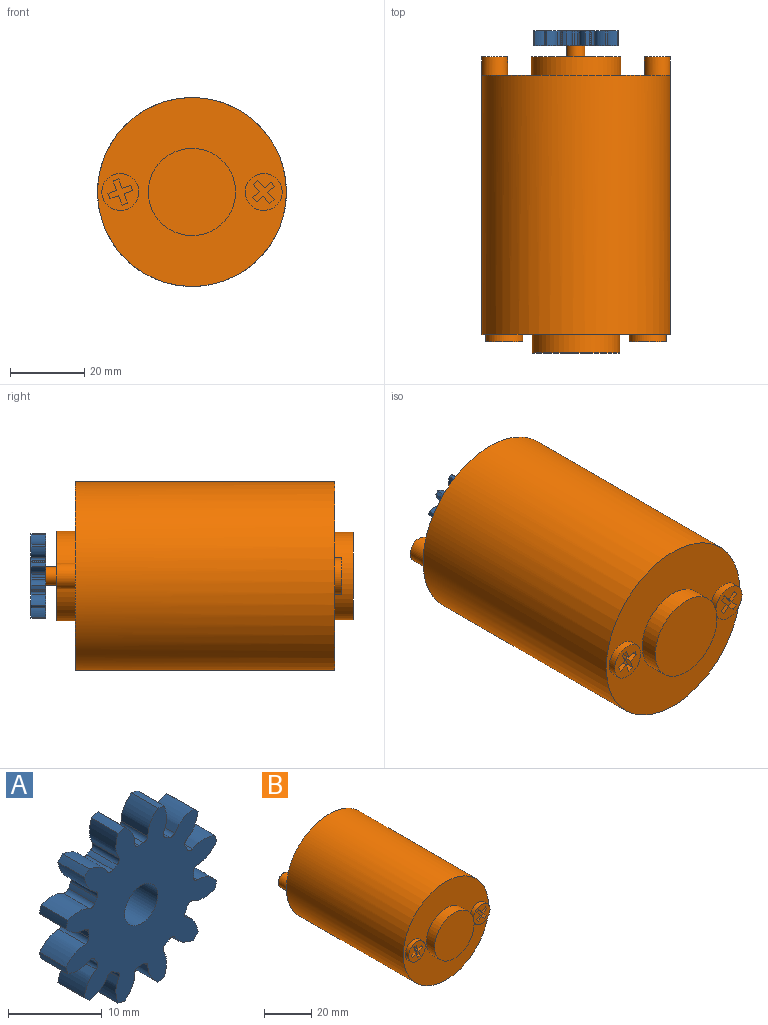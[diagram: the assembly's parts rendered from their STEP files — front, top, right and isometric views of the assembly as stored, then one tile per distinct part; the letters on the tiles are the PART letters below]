
ASSEMBLY  parts=2 mates=1
PART A: 75 faces, bbox 22.8x4x22.8 mm
  f0: extruded ~4x2.94mm, area 13.7mm2, adj f48,f49,f50,f51
  f1: cylinder r=7.92mm len=4mm, axis (0,1,0), area 2.8mm2, adj f49,f50,f51,f52
  f2: extruded ~4x2.94mm, area 13.7mm2, adj f3,f49,f50,f52
  f3: cylinder r=11.67mm len=4mm, axis (0,1,0), area 4.1mm2, adj f2,f4,f49,f50
  f4: extruded ~4x3.32mm, area 13.7mm2, adj f3,f49,f50,f53
  f5: cylinder r=7.92mm len=4mm, axis (0,1,0), area 2.8mm2, adj f49,f50,f53,f54
  f6: extruded ~4x2.8mm, area 13.7mm2, adj f7,f49,f50,f54
  f7: cylinder r=11.67mm len=4mm, axis (0,1,0), area 4.1mm2, adj f6,f8,f49,f50
  f8: extruded ~4x2.8mm, area 13.7mm2, adj f7,f49,f50,f55
  f9: cylinder r=7.92mm len=4mm, axis (0,1,0), area 2.8mm2, adj f49,f50,f55,f56
  f10: extruded ~4x3.32mm, area 13.7mm2, adj f11,f49,f50,f56
  f11: cylinder r=11.67mm len=4mm, axis (0,1,0), area 4.1mm2, adj f10,f12,f49,f50
  f12: extruded ~4x2.94mm, area 13.7mm2, adj f11,f49,f50,f57
  f13: cylinder r=7.92mm len=4mm, axis (0,1,0), area 2.8mm2, adj f49,f50,f57,f58
  f14: extruded ~4x2.94mm, area 13.7mm2, adj f15,f49,f50,f58
  f15: cylinder r=11.67mm len=4mm, axis (0,1,0), area 4.1mm2, adj f14,f16,f49,f50
  f16: extruded ~4x3.32mm, area 13.7mm2, adj f15,f49,f50,f59
  f17: cylinder r=7.92mm len=4mm, axis (0,1,0), area 2.8mm2, adj f49,f50,f59,f60
  f18: extruded ~4x2.8mm, area 13.7mm2, adj f19,f49,f50,f60
  f19: cylinder r=11.67mm len=4mm, axis (0,1,0), area 4.1mm2, adj f18,f20,f49,f50
  f20: extruded ~4x2.8mm, area 13.7mm2, adj f19,f49,f50,f61
  f21: cylinder r=7.92mm len=4mm, axis (0,1,0), area 2.8mm2, adj f49,f50,f61,f62
  f22: extruded ~4x3.32mm, area 13.7mm2, adj f23,f49,f50,f62
  f23: cylinder r=11.67mm len=4mm, axis (0,1,0), area 4.1mm2, adj f22,f24,f49,f50
  f24: extruded ~4x2.94mm, area 13.7mm2, adj f23,f49,f50,f63
  f25: cylinder r=7.92mm len=4mm, axis (0,1,0), area 2.8mm2, adj f49,f50,f63,f64
  f26: extruded ~4x2.94mm, area 13.7mm2, adj f27,f49,f50,f64
  f27: cylinder r=11.67mm len=4mm, axis (0,1,0), area 4.1mm2, adj f26,f28,f49,f50
  f28: extruded ~4x3.32mm, area 13.7mm2, adj f27,f49,f50,f65
  f29: cylinder r=7.92mm len=4mm, axis (0,1,0), area 2.8mm2, adj f49,f50,f65,f66
  f30: extruded ~4x2.8mm, area 13.7mm2, adj f31,f49,f50,f66
  f31: cylinder r=11.67mm len=4mm, axis (0,1,0), area 4.1mm2, adj f30,f32,f49,f50
  f32: extruded ~4x2.8mm, area 13.7mm2, adj f31,f49,f50,f67
  f33: cylinder r=7.92mm len=4mm, axis (0,1,0), area 2.8mm2, adj f49,f50,f67,f68
  f34: extruded ~4x3.32mm, area 13.7mm2, adj f35,f49,f50,f68
  f35: cylinder r=11.67mm len=4mm, axis (0,1,0), area 4.1mm2, adj f34,f36,f49,f50
  f36: extruded ~4x2.94mm, area 13.7mm2, adj f35,f49,f50,f69
  f37: cylinder r=7.92mm len=4mm, axis (0,1,0), area 2.8mm2, adj f49,f50,f69,f70
  f38: extruded ~4x2.94mm, area 13.7mm2, adj f39,f49,f50,f70
  f39: cylinder r=11.67mm len=4mm, axis (0,1,0), area 4.1mm2, adj f38,f40,f49,f50
  f40: extruded ~4x3.32mm, area 13.7mm2, adj f39,f49,f50,f71
  f41: cylinder r=7.92mm len=4mm, axis (0,1,0), area 2.8mm2, adj f49,f50,f71,f72
  f42: extruded ~4x2.8mm, area 13.7mm2, adj f43,f49,f50,f72
  f43: cylinder r=11.67mm len=4mm, axis (0,1,0), area 4.1mm2, adj f42,f44,f49,f50
  f44: extruded ~4x2.8mm, area 13.7mm2, adj f43,f49,f50,f73
  f45: cylinder r=7.92mm len=4mm, axis (0,1,0), area 2.8mm2, adj f49,f50,f73,f74
  f46: extruded ~4x3.32mm, area 13.7mm2, adj f48,f49,f50,f74
  f47: cylinder r=2.5mm len=5mm, axis (0,1,0), area 62.8mm2, adj f49,f50
  f48: cylinder r=11.67mm len=4mm, axis (0,1,0), area 4.1mm2, adj f0,f46,f49,f50
  f49: plane 22.85x22.85mm, normal (0,-1,0), area 282.5mm2, adj f0,f1,f2,f3,f4,f5,f6,f7
  f50: plane 22.85x22.85mm, normal (0,1,0), area 282.5mm2, adj f0,f1,f2,f3,f4,f5,f6,f7
  f51: cylinder r=0.61mm len=4mm, axis (0,1,0), area 3.7mm2, adj f0,f1,f49,f50
  f52: cylinder r=0.61mm len=4mm, axis (0,1,0), area 3.7mm2, adj f1,f2,f49,f50
  f53: cylinder r=0.61mm len=4mm, axis (0,1,0), area 3.7mm2, adj f4,f5,f49,f50
  f54: cylinder r=0.61mm len=4mm, axis (0,1,0), area 3.7mm2, adj f5,f6,f49,f50
  f55: cylinder r=0.61mm len=4mm, axis (0,1,0), area 3.7mm2, adj f8,f9,f49,f50
  f56: cylinder r=0.61mm len=4mm, axis (0,1,0), area 3.7mm2, adj f9,f10,f49,f50
  f57: cylinder r=0.61mm len=4mm, axis (0,1,0), area 3.7mm2, adj f12,f13,f49,f50
  f58: cylinder r=0.61mm len=4mm, axis (0,1,0), area 3.7mm2, adj f13,f14,f49,f50
  f59: cylinder r=0.61mm len=4mm, axis (0,1,0), area 3.7mm2, adj f16,f17,f49,f50
  f60: cylinder r=0.61mm len=4mm, axis (0,1,0), area 3.7mm2, adj f17,f18,f49,f50
  f61: cylinder r=0.61mm len=4mm, axis (0,1,0), area 3.7mm2, adj f20,f21,f49,f50
  f62: cylinder r=0.61mm len=4mm, axis (0,1,0), area 3.7mm2, adj f21,f22,f49,f50
  f63: cylinder r=0.61mm len=4mm, axis (0,1,0), area 3.7mm2, adj f24,f25,f49,f50
  f64: cylinder r=0.61mm len=4mm, axis (0,1,0), area 3.7mm2, adj f25,f26,f49,f50
  f65: cylinder r=0.61mm len=4mm, axis (0,1,0), area 3.7mm2, adj f28,f29,f49,f50
  f66: cylinder r=0.61mm len=4mm, axis (0,1,0), area 3.7mm2, adj f29,f30,f49,f50
  f67: cylinder r=0.61mm len=4mm, axis (0,1,0), area 3.7mm2, adj f32,f33,f49,f50
  f68: cylinder r=0.61mm len=4mm, axis (0,1,0), area 3.7mm2, adj f33,f34,f49,f50
  f69: cylinder r=0.61mm len=4mm, axis (0,1,0), area 3.7mm2, adj f36,f37,f49,f50
  f70: cylinder r=0.61mm len=4mm, axis (0,1,0), area 3.7mm2, adj f37,f38,f49,f50
  f71: cylinder r=0.61mm len=4mm, axis (0,1,0), area 3.7mm2, adj f40,f41,f49,f50
  f72: cylinder r=0.61mm len=4mm, axis (0,1,0), area 3.7mm2, adj f41,f42,f49,f50
  f73: cylinder r=0.61mm len=4mm, axis (0,1,0), area 3.7mm2, adj f44,f45,f49,f50
  f74: cylinder r=0.61mm len=4mm, axis (0,1,0), area 3.7mm2, adj f45,f46,f49,f50
PART B: 43 faces, bbox 51x87x51 mm
  f0: plane 51x51mm, normal (0,-1,0), area 1449.5mm2, adj f1,f3,f24,f40
  f1: cylinder r=25.5mm len=70mm, axis (0,1,0), area 11215.5mm2, adj f0,f2
  f2: plane 51x51mm, normal (0,1,0), area 1507.5mm2, adj f1,f5,f7,f9
  f3: cylinder r=11.79mm len=23.58mm, axis (0,1,0), area 370.4mm2, adj f0,f4
  f4: plane 23.58x23.58mm, normal (0,-1,0), area 436.8mm2, adj f3
  f5: cylinder r=12.08mm len=24.16mm, axis (0,-1,0), area 379.5mm2, adj f2,f6
  f6: plane 24.16x24.16mm, normal (0,1,0), area 438.7mm2, adj f5,f11
  f7: cylinder r=3.5mm len=7mm, axis (0,-1,0), area 110mm2, adj f2,f8
  f8: plane 7x7mm, normal (0,1,0), area 38.5mm2, adj f7
  f9: cylinder r=3.5mm len=7mm, axis (0,-1,0), area 110mm2, adj f2,f10
  f10: plane 7x7mm, normal (0,1,0), area 38.5mm2, adj f9
  f11: cylinder r=2.5mm len=7mm, axis (0,-1,0), area 110mm2, adj f6,f12
  f12: plane 5x5mm, normal (0,1,0), area 19.6mm2, adj f11
  f13: plane 2x1.16mm, normal (-0.77,0,-0.64), area 3mm2, adj f14,f25,f26,f27
  f14: plane 2x1.91mm, normal (-0.64,0,0.77), area 5mm2, adj f13,f15,f26,f27
  f15: plane 2.09x2mm, normal (-0.77,0,-0.64), area 5.4mm2, adj f14,f16,f26,f27
  f16: plane 2x1.21mm, normal (-0.64,0,0.77), area 3.2mm2, adj f15,f17,f26,f27
  f17: plane 2.09x2mm, normal (0.77,0,0.64), area 5.4mm2, adj f16,f18,f26,f27
  f18: plane 2x1.91mm, normal (-0.64,0,0.77), area 5mm2, adj f17,f19,f26,f27
  f19: plane 2x1.16mm, normal (0.77,0,0.64), area 3mm2, adj f18,f20,f26,f27
  f20: plane 2x1.91mm, normal (0.64,0,-0.77), area 5mm2, adj f19,f21,f26,f27
  f21: plane 2.09x2mm, normal (0.77,0,0.64), area 5.4mm2, adj f20,f22,f26,f27
  f22: plane 2x1.21mm, normal (0.64,0,-0.77), area 3.2mm2, adj f21,f23,f26,f27
  f23: plane 2.09x2mm, normal (-0.77,0,-0.64), area 5.4mm2, adj f22,f25,f26,f27
  f24: cylinder r=4.99mm len=9.98mm, axis (0,1,0), area 62.7mm2, adj f0,f26
  f25: plane 2x1.91mm, normal (0.64,0,-0.77), area 5mm2, adj f13,f23,f26,f27
  f26: plane 9.98x9.98mm, normal (0,-1,0), area 59.8mm2, adj f13,f14,f15,f16,f17,f18,f19,f20
  f27: plane 6.34x6.01mm, normal (0,-1,0), area 18.5mm2, adj f13,f14,f15,f16,f17,f18,f19,f20
  f28: plane 2.35x2mm, normal (-0.34,0,0.94), area 5mm2, adj f29,f39,f41,f42
  f29: plane 2x1.42mm, normal (0.94,0,0.34), area 3mm2, adj f28,f30,f41,f42
  f30: plane 2.35x2mm, normal (0.34,0,-0.94), area 5mm2, adj f29,f31,f41,f42
  f31: plane 2.56x2mm, normal (0.94,0,0.34), area 5.4mm2, adj f30,f32,f41,f42
  f32: plane 2x1.48mm, normal (0.34,0,-0.94), area 3.2mm2, adj f31,f33,f41,f42
  f33: plane 2.56x2mm, normal (-0.94,0,-0.34), area 5.4mm2, adj f32,f34,f41,f42
  f34: plane 2.35x2mm, normal (0.34,0,-0.94), area 5mm2, adj f33,f35,f41,f42
  f35: plane 2x1.42mm, normal (-0.94,0,-0.34), area 3mm2, adj f34,f36,f41,f42
  f36: plane 2.35x2mm, normal (-0.34,0,0.94), area 5mm2, adj f35,f37,f41,f42
  f37: plane 2.56x2mm, normal (-0.94,0,-0.34), area 5.4mm2, adj f36,f38,f41,f42
  f38: plane 2x1.48mm, normal (-0.34,0,0.94), area 3.2mm2, adj f37,f39,f41,f42
  f39: plane 2.56x2mm, normal (0.94,0,0.34), area 5.4mm2, adj f28,f38,f41,f42
  f40: cylinder r=4.99mm len=9.98mm, axis (0,1,0), area 62.7mm2, adj f0,f41
  f41: plane 9.98x9.98mm, normal (0,-1,0), area 59.8mm2, adj f28,f29,f30,f31,f32,f33,f34,f35
  f42: plane 7.08x6.69mm, normal (0,-1,0), area 18.5mm2, adj f28,f29,f30,f31,f32,f33,f34,f35
PLACE A t=(-37.39,12.58,-14)mm
PLACE B t=(-37.39,0.58,-14)mm
MATE revolute A.f3 <-> B.f1  axis (0,1,0) through (-37.39,12.58,-14)mm
